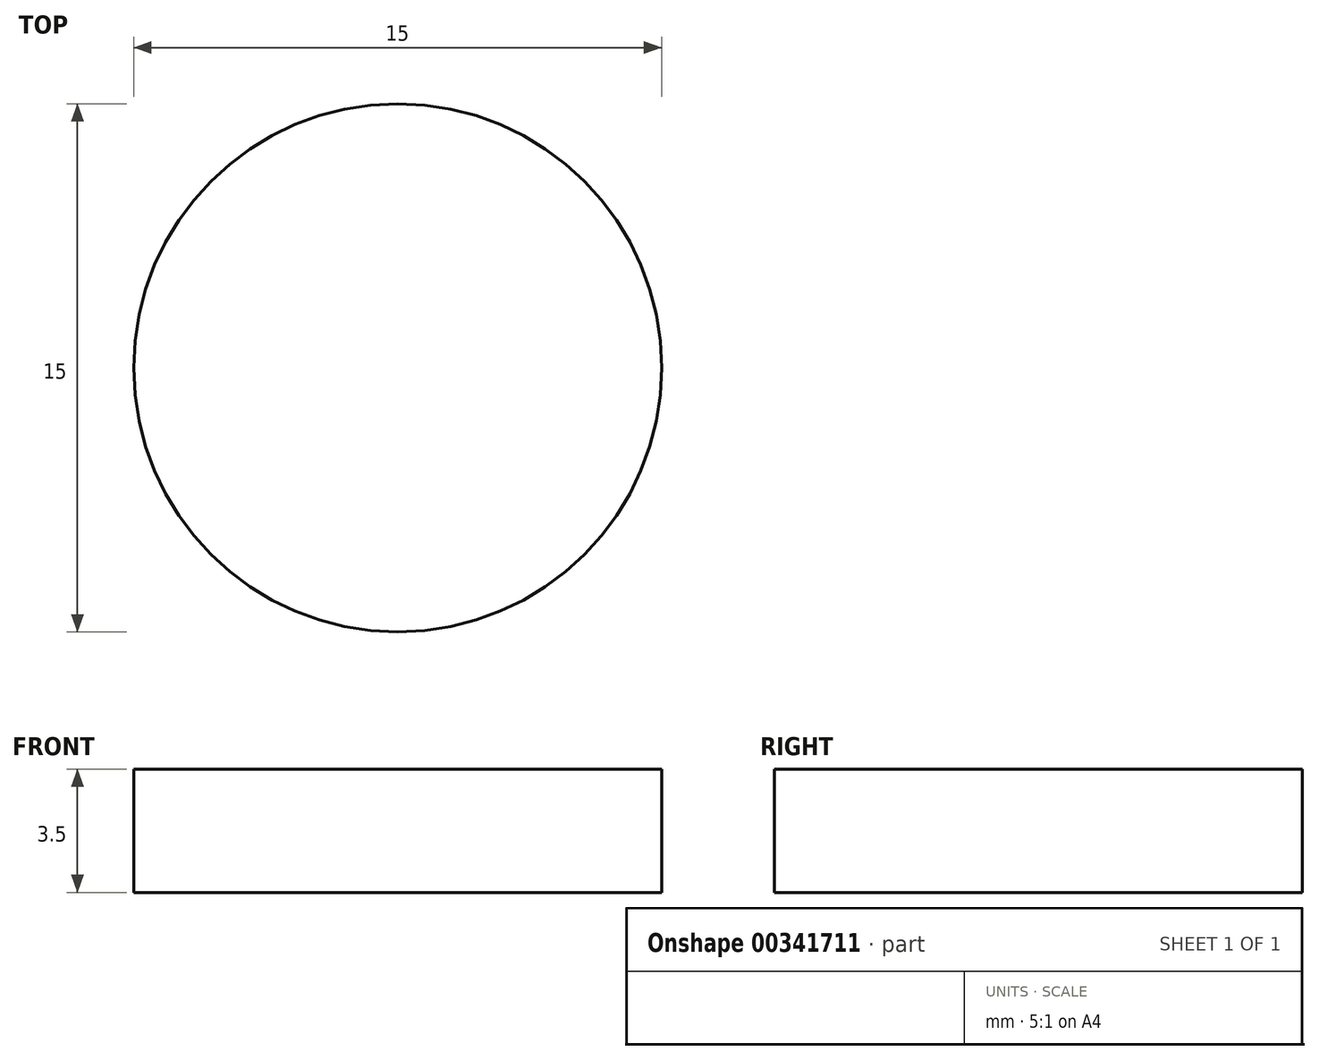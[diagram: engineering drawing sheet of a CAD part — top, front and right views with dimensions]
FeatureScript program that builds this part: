
annotation { "Feature Type Name" : "Feature", "Feature Type Description" : "" }
export const myFeature = defineFeature(function(context is Context, id is Id, definition is map)
    precondition{}
    {
        {
            var Q0;
            Q0=qCreatedBy(makeId("Top.planeOp"),FACE);
            var sketch = newSketch(context, id + "F0", { "sketchPlane" : qUnion([Q0])});
            skCircle(sketch, "E0", {"center": v(0, 0) * mm, "radius": 7.5 * mm});
            skSolve(sketch);
        }
        {
            var Q0;
            Q0=makeQuery(id+"F0.imprint","IMPRINT",FACE,{"disambiguationData":[TD([[makeQuery(id+"F0.imprint","IMPRINT",EDGE,{"derivedFrom":sQuery(id+"F0.wireOp",EDGE,"E0")}),1.0]])]});
            extrude(context, id + "F1", {"entities" : qUnion([Q0]), "depth" : 3.5 * mm});
        }
    });
